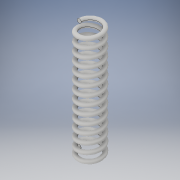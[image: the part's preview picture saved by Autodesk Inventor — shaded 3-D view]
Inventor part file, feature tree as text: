
AUTODESK INVENTOR PART (.ipt)
format: ipt  version: 2018 (Build 220112000, 112)  size: 521,216 bytes
history: native  units: in
note: dims shown in document units (in); Inventor stores cm internally (conversion verified against a paired STEP export)
features: helix x1, sketch x1
ambient origin geometry x8: Origin, YZ Plane, XZ Plane, XY Plane, X Axis, Y Axis, Z Axis, Center Point
bodies: Solid1 (feature_tree)
feature tree (2):
  helix  "Coil1"  [1 undecoded]
  sketch  "Sketch1"  dims[d1=0.059in d2=1.0in d3=0.5in d4=5.1181in d5=0.0in d6=90.0deg d7=90.0deg d8=90.0deg d9=90.0deg]
note: 1 required parameter value undecoded (feature->parameter linkage not recoverable at this tier; creation-order binding heuristic only, values carry confidence <= 0.55)
